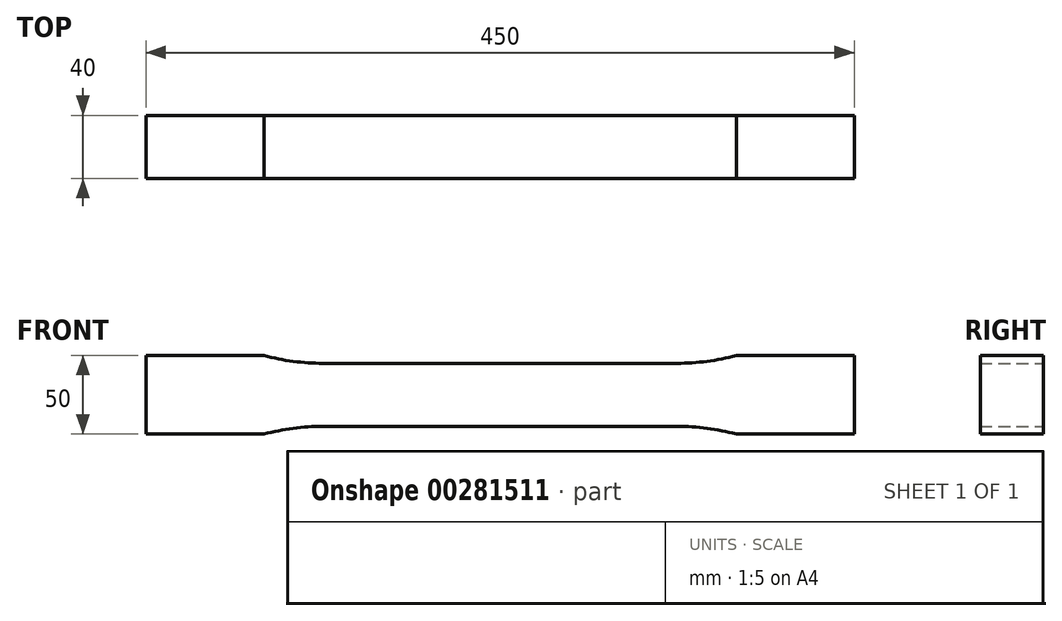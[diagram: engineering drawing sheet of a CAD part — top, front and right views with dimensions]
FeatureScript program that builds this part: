
annotation { "Feature Type Name" : "Feature", "Feature Type Description" : "" }
export const myFeature = defineFeature(function(context is Context, id is Id, definition is map)
    precondition{}
    {
        {
            var Q0;
            Q0=qCreatedBy(makeId("Front.planeOp"),FACE);
            var sketch = newSketch(context, id + "F0", { "sketchPlane" : qUnion([Q0])});
            skLineSegment(sketch, "E0", {"start": v(0, 20) * mm, "end": v(112.5, 20) * mm});
            skLineSegment(sketch, "E1", {"start": v(150, 25) * mm, "end": v(225, 25) * mm});
            skLineSegment(sketch, "E2", {"start": v(225, 25) * mm, "end": v(225, 0) * mm});
            skLineSegment(sketch, "E3.MirrorCS", {"start": v(0, -20) * mm, "end": v(112.5, -20) * mm});
            skLineSegment(sketch, "E4.MirrorCS", {"start": v(225, -25) * mm, "end": v(225, 0) * mm});
            skLineSegment(sketch, "E5.MirrorCS", {"start": v(150, -25) * mm, "end": v(225, -25) * mm});
            skLineSegment(sketch, "E6.MirrorCS", {"start": v(-150, -25) * mm, "end": v(-225, -25) * mm});
            skLineSegment(sketch, "E7.MirrorCS", {"start": v(-150, 25) * mm, "end": v(-225, 25) * mm});
            skLineSegment(sketch, "E8.MirrorCS", {"start": v(-225, -25) * mm, "end": v(-225, 0) * mm});
            skLineSegment(sketch, "E9.MirrorCS", {"start": v(0, -20) * mm, "end": v(-112.5, -20) * mm});
            skLineSegment(sketch, "E10.MirrorCS", {"start": v(-225, 25) * mm, "end": v(-225, 0) * mm});
            skLineSegment(sketch, "E11.MirrorCS", {"start": v(0, 20) * mm, "end": v(-112.5, 20) * mm});
            skArc(sketch, "E12", {"start": v(-112.5, 20) * mm, "mid": v(-131.42, 21.26) * mm, "end": v(-150, 25) * mm});
            skArc(sketch, "E13", {"start": v(-112.5, -20) * mm, "mid": v(-131.42, -21.26) * mm, "end": v(-150, -25) * mm});
            skArc(sketch, "E14", {"start": v(112.5, 20) * mm, "mid": v(131.42, 21.26) * mm, "end": v(150, 25) * mm});
            skArc(sketch, "E15", {"start": v(112.5, -20) * mm, "mid": v(131.42, -21.26) * mm, "end": v(150, -25) * mm});
            skSolve(sketch);
        }
        {
            var Q0;
            Q0=makeQuery(id+"F0.imprint","IMPRINT",FACE,{"disambiguationData":[TD([[makeQuery(id+"F0.imprint","IMPRINT",EDGE,{"derivedFrom":sQuery(id+"F0.wireOp",EDGE,"E0")}),-1.0]])]});
            extrude(context, id + "F1", {"entities" : qUnion([Q0]), "endBound" : BoundingType.SYMMETRIC, "depth" : 40 * mm});
        }
    });
